# Revit family: Ридан_BVR-DR_Кран шаровой ГОСТ полнопроходной со спускным элементом
name_source: partatom
category: Арматура трубопроводов
units: mm (PartAtom-declared; Revit-internal decimal feet)

## family parameters
Всегда вертикально = Да
На основе рабочей плоскости = Нет
Общий = Нет
При загрузке вырезать с полостями = Нет
Размер круглого соединителя = Использовать диаметр
Тип детали = Вставляется

## types (6) — shared parameters
ADSK_Версия Revit = 2019
ADSK_Версия семейства = 1.0
ADSK_Единица измерения = шт.
ADSK_Завод-изготовитель = ООО «Ридан-Трейд»
ADSK_Количество = 1
ADSK_Материал = Латунь никелированная
ADSK_Потеря давления жидкости = 0.0 Па
ADSK_Расход жидкости = 0.0000 м³/ч
LT = BVR-DR
URL = https://ridan.ru
n = 15 мм
q = 11 мм
r = 4 мм
s = 5 мм
t = 5 мм
u = 12 мм
v = 16 мм
w = 9 мм

## per-type parameters (varying)
| type | ADSK_Диаметр условный | ADSK_Код изделия | ADSK_Марка | ADSK_Масса | ADSK_Наименование | ADSK_Пропускная способность | a | b | c | d | e | f | g | h | i | j | k | l | m | o | p | x | y | УГО_Длина |
| DN15 | 15 мм | 065B8316RG | BVR-DR DN15 | 0.27 | Кран шаровой ГОСТ BVR-DR полнопроходной с внутренней резьбой со спускным элементом PN40, Tmax=110C, DN15 | 15.0000 м³/ч | 21 мм | 12 мм | 8 мм | 7 мм | 11 мм | 16 мм | 11 мм | 29 мм | 27 мм | 29 мм | 17 мм | 31 мм | 25 мм | 20 мм | 20 мм | 19 мм | 27 мм | 27 мм |
| DN20 | 20 мм | 065B8317RG | BVR-DR DN20 | 0.36 | Кран шаровой ГОСТ BVR-DR полнопроходной с внутренней резьбой со спускным элементом PN40, Tmax=110C, DN20 | 28.0000 м³/ч | 18 мм | 21 мм | 8 мм | 5 мм | 14 мм | 18 мм | 17 мм | 35 мм | 33 мм | 32 мм | 17 мм | 37 мм | 30 мм | 23 мм | 23 мм | 24 мм | 34 мм | 34 мм |
| DN25 | 25 мм | 065B8318RG | BVR-DR DN25 | 0.56 | Кран шаровой ГОСТ BVR-DR полнопроходной с внутренней резьбой со спускным элементом PN40, Tmax=110C, DN25 | 39.0000 м³/ч | 25 мм | 21 мм | 7 мм | 7 мм | 16 мм | 21 мм | 15 мм | 42 мм | 40 мм | 38 мм | 19 мм | 44 мм | 37 мм | 27 мм | 27 мм | 30 мм | 34 мм | 34 мм |
| DN32 | 32 мм | 065B8319RG | BVR-DR DN32 | 0.73 | Кран шаровой ГОСТ BVR-DR полнопроходной с внутренней резьбой со спускным элементом PN40, Tmax=110C, DN32 | 84.0000 м³/ч | 28 мм | 26 мм | 8 мм | 7 мм | 18 мм | 25 мм | 18 мм | 52 мм | 50 мм | 45 мм | 23 мм | 55 мм | 46 мм | 32 мм | 32 мм | 39 мм | 40 мм | 40 мм |
| DN40 | 40 мм | 065B8320RG | BVR-DR DN40 | 1.12 | Кран шаровой ГОСТ BVR-DR полнопроходной с внутренней резьбой со спускным элементом PN40, Tmax=110C, DN40 | 156.0000 м³/ч | 27 мм | 38 мм | 8 мм | 7 мм | 19 мм | 29 мм | 25 мм | 62 мм | 60 мм | 50 мм | 24 мм | 65 мм | 53 мм | 38 мм | 38 мм | 45 мм | 52 мм | 52 мм |
| DN50 | 50 мм | 065B8321RG | BVR-DR DN50 | 1.7 | Кран шаровой ГОСТ BVR-DR полнопроходной с внутренней резьбой со спускным элементом PN40, Tmax=110C, DN50 | 243.0000 м³/ч | 31 мм | 43 мм | 9 мм | 11 мм | 22 мм | 35 мм | 29 мм | 77 мм | 75 мм | 60 мм | 26 мм | 80 мм | 65 мм | 41 мм | 41 мм | 57 мм | 63 мм | 63 мм |
